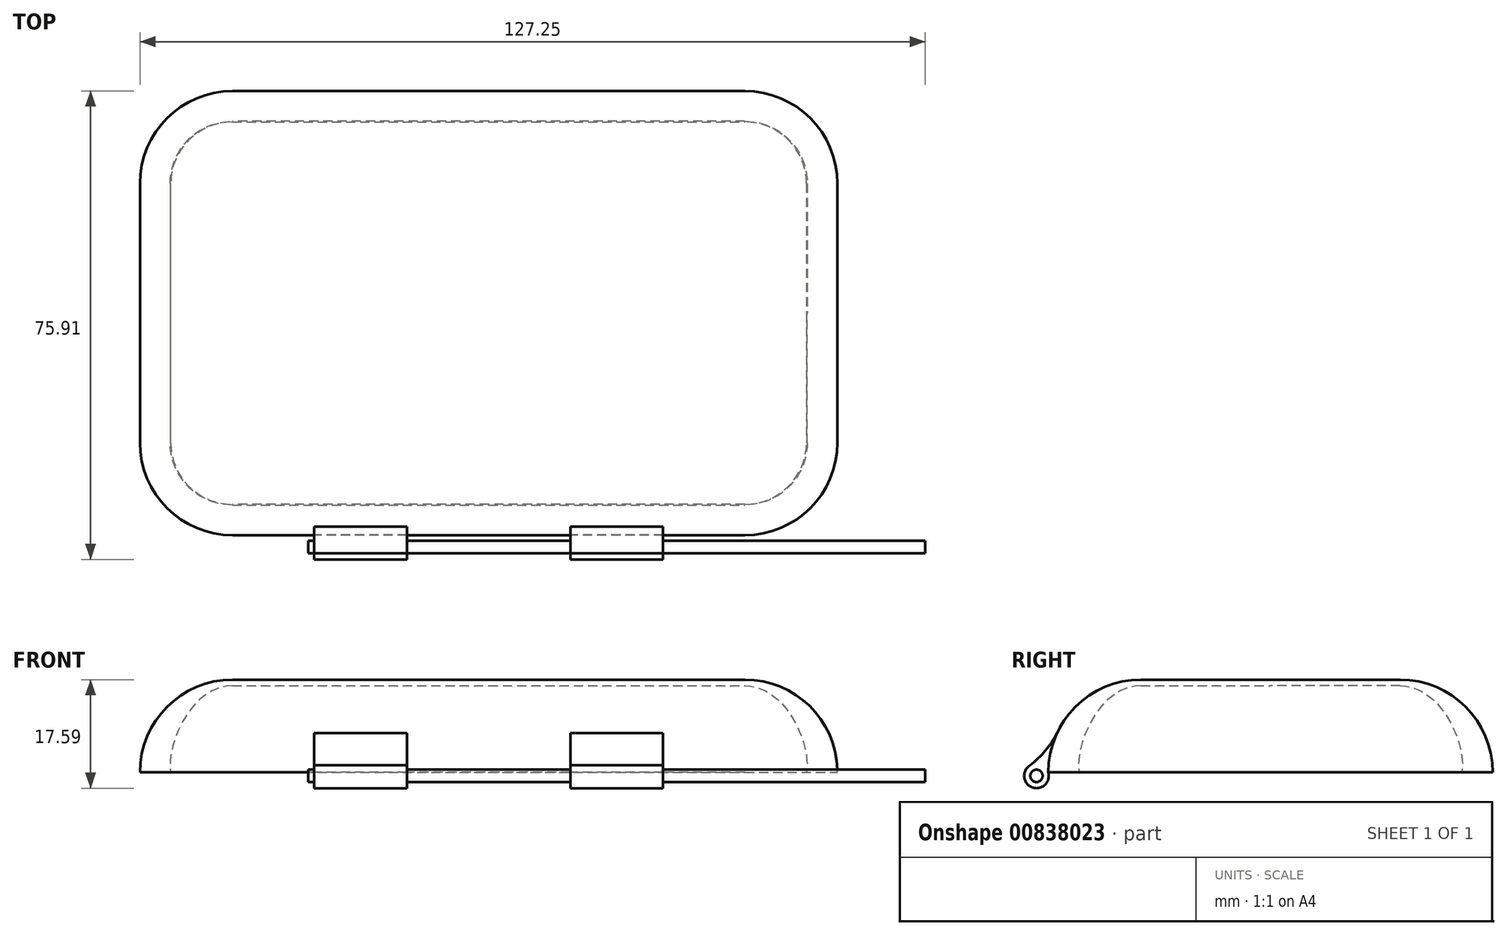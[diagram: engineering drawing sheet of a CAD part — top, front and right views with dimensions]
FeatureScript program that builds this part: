
annotation { "Feature Type Name" : "Feature", "Feature Type Description" : "" }
export const myFeature = defineFeature(function(context is Context, id is Id, definition is map)
    precondition{}
    {
        {
            var Q0;
            Q0=qCreatedBy(makeId("Top.planeOp"),FACE);
            var sketch = newSketch(context, id + "F0", { "sketchPlane" : qUnion([Q0])});
            skLineSegment(sketch, "E0", {"start": v(0, 0) * mm, "end": v(0, 27) * mm, "construction": true});
            skLineSegment(sketch, "E1", {"start": v(0, 27) * mm, "end": v(41.5, 27) * mm});
            skLineSegment(sketch, "E2", {"start": v(47.5, 21) * mm, "end": v(47.5, 0) * mm});
            skLineSegment(sketch, "E3", {"start": v(47.5, 0) * mm, "end": v(0, 0) * mm, "construction": true});
            skLineSegment(sketch, "E4.MirrorCS", {"start": v(0, 27) * mm, "end": v(-41.5, 27) * mm});
            skLineSegment(sketch, "E5.MirrorCS", {"start": v(-47.5, 21) * mm, "end": v(-47.5, 0) * mm});
            skLineSegment(sketch, "E6.MirrorCS", {"start": v(0, -27) * mm, "end": v(-41.5, -27) * mm});
            skLineSegment(sketch, "E7.MirrorCS", {"start": v(0, -27) * mm, "end": v(41.5, -27) * mm});
            skLineSegment(sketch, "E8.MirrorCS", {"start": v(47.5, -21) * mm, "end": v(47.5, 0) * mm});
            skLineSegment(sketch, "E9.MirrorCS", {"start": v(-47.5, -21) * mm, "end": v(-47.5, 0) * mm});
            skPoint(sketch, "E10.visualSharp", {"position": v(47.5, 27) * mm});
            skArc(sketch, "E10.filletArc", {"start": v(47.5, 21) * mm, "mid": v(45.74, 25.24) * mm, "end": v(41.5, 27) * mm});
            skPoint(sketch, "E11.visualSharp", {"position": v(-47.5, 27) * mm});
            skArc(sketch, "E11.filletArc", {"start": v(-41.5, 27) * mm, "mid": v(-45.74, 25.24) * mm, "end": v(-47.5, 21) * mm});
            skPoint(sketch, "E12.visualSharp", {"position": v(-47.5, -27) * mm});
            skArc(sketch, "E12.filletArc", {"start": v(-47.5, -21) * mm, "mid": v(-45.74, -25.24) * mm, "end": v(-41.5, -27) * mm});
            skPoint(sketch, "E13.visualSharp", {"position": v(47.5, -27) * mm});
            skArc(sketch, "E13.filletArc", {"start": v(41.5, -27) * mm, "mid": v(45.74, -25.24) * mm, "end": v(47.5, -21) * mm});
            skLineSegment(sketch, "E14.0", {"start": v(0, 31) * mm, "end": v(-41.5, 31) * mm});
            skArc(sketch, "E14.1", {"start": v(41.5, -31) * mm, "mid": v(48.57, -28.07) * mm, "end": v(51.5, -21) * mm});
            skLineSegment(sketch, "E14.2", {"start": v(51.5, -21) * mm, "end": v(51.5, 0) * mm});
            skLineSegment(sketch, "E14.3", {"start": v(51.5, 21) * mm, "end": v(51.5, 0) * mm});
            skArc(sketch, "E14.4", {"start": v(51.5, 21) * mm, "mid": v(48.57, 28.07) * mm, "end": v(41.5, 31) * mm});
            skLineSegment(sketch, "E14.5", {"start": v(0, -31) * mm, "end": v(41.5, -31) * mm});
            skLineSegment(sketch, "E14.6", {"start": v(0, 31) * mm, "end": v(41.5, 31) * mm});
            skLineSegment(sketch, "E14.7", {"start": v(0, -31) * mm, "end": v(-41.5, -31) * mm});
            skArc(sketch, "E14.8", {"start": v(-51.5, -21) * mm, "mid": v(-48.57, -28.07) * mm, "end": v(-41.5, -31) * mm});
            skLineSegment(sketch, "E14.9", {"start": v(-51.5, -21) * mm, "end": v(-51.5, 0) * mm});
            skLineSegment(sketch, "E14.10", {"start": v(-51.5, 21) * mm, "end": v(-51.5, 0) * mm});
            skArc(sketch, "E14.11", {"start": v(-41.5, 31) * mm, "mid": v(-48.57, 28.07) * mm, "end": v(-51.5, 21) * mm});
            skLineSegment(sketch, "E15", {"start": v(41.5, -21) * mm, "end": v(41.5, 21) * mm});
            skLineSegment(sketch, "E16", {"start": v(41.5, 21) * mm, "end": v(-41.5, 21) * mm});
            skLineSegment(sketch, "E17", {"start": v(-41.5, 21) * mm, "end": v(-41.5, -21) * mm});
            skLineSegment(sketch, "E18", {"start": v(-41.5, -21) * mm, "end": v(41.5, -21) * mm});
            skSolve(sketch);
        }
        {
            var Q0;
            Q0=qCreatedBy(makeId("Front.planeOp"),FACE);
            var sketch = newSketch(context, id + "F1", { "sketchPlane" : qUnion([Q0])});
            skArc(sketch, "E19", {"start": v(56.5, 0) * mm, "mid": v(52.1, 10.6) * mm, "end": v(41.5, 15) * mm});
            skFitSpline(sketch, "E20", {"points": [v(41.5, 14) * mm, v(51.5, 0) * mm, v(41.5, -12.07) * mm], "startDerivative": vector(40.14, 0) * mm, "endDerivative": vector(-25.73, -56.42) * mm});
            skLineSegment(sketch, "E21", {"start": v(41.5, 15) * mm, "end": v(41.5, 14) * mm});
            skLineSegment(sketch, "E22", {"start": v(41.5, 14) * mm, "end": v(41.5, 0) * mm, "construction": true});
            skLineSegment(sketch, "E23", {"start": v(56.5, 0) * mm, "end": v(51.5, 0) * mm});
            skSolve(sketch);
        }
        {
            var Q0;
            Q0=makeQuery(id+"F1.imprint","IMPRINT",FACE,{"disambiguationData":[TD([[makeQuery(id+"F1.imprint","IMPRINT",EDGE,{"derivedFrom":sQuery(id+"F1.wireOp",EDGE,"E19")}),1.0]])]});
            var Q1;
            Q1=sQuery(id+"F0.wireOp",EDGE,"E14.2");
            var Q2;
            Q2=sQuery(id+"F0.wireOp",EDGE,"E14.1");
            var Q3;
            Q3=sQuery(id+"F0.wireOp",EDGE,"E14.5");
            var Q4;
            Q4=sQuery(id+"F0.wireOp",EDGE,"E14.7");
            var Q5;
            Q5=sQuery(id+"F0.wireOp",EDGE,"E14.8");
            var Q6;
            Q6=sQuery(id+"F0.wireOp",EDGE,"E14.9");
            var Q7;
            Q7=sQuery(id+"F0.wireOp",EDGE,"E14.10");
            var Q8;
            Q8=sQuery(id+"F0.wireOp",EDGE,"E14.11");
            var Q9;
            Q9=sQuery(id+"F0.wireOp",EDGE,"E14.0");
            var Q10;
            Q10=sQuery(id+"F0.wireOp",EDGE,"E14.6");
            var Q11;
            Q11=sQuery(id+"F0.wireOp",EDGE,"E14.4");
            var Q12;
            Q12=sQuery(id+"F0.wireOp",EDGE,"E14.3");
            sweep(context, id + "F2", {"profiles" : qUnion([Q0]), "path" : qUnion([Q1, Q2, Q3, Q4, Q5, Q6, Q7, Q8, Q9, Q10, Q11, Q12])});
        }
        {
            var Q0;
            Q0=makeQuery(id+"F0.imprint","IMPRINT",FACE,{"disambiguationData":[TD([[makeQuery(id+"F0.imprint","IMPRINT",EDGE,{"derivedFrom":sQuery(id+"F0.wireOp",EDGE,"E15")}),1.0]])]});
            extrude(context, id + "F3", {"entities" : qUnion([Q0]), "operationType" : NewBodyOperationType.ADD, "depth" : 15 * mm, "offsetDistance" : 25 * mm, "hasSecondDirection" : true, "secondDirectionOppositeDirection" : false, "secondDirectionDepth" : 14 * mm});
        }
        {
            var Q0;
            Q0=makeQuery(id+"F3.opExtrude","CAP_FACE",FACE,{"disambiguationData":[OSD([sQuery(id+"F0.wireOp",EDGE,"E15"),sQuery(id+"F0.wireOp",EDGE,"E16"),sQuery(id+"F0.wireOp",EDGE,"E17"),sQuery(id+"F0.wireOp",EDGE,"E18")])],"isStart":false});
            var sketch = newSketch(context, id + "F4", { "sketchPlane" : qUnion([Q0])});
            skLineSegment(sketch, "E24", {"start": v(-41.5, -21) * mm, "end": v(0, -21) * mm, "construction": true});
            skPoint(sketch, "E25", {"position": v(0, -21) * mm});
            skPoint(sketch, "E26", {"position": v(-20.75, -21) * mm});
            skLineSegment(sketch, "E27", {"start": v(0, -21) * mm, "end": v(41.5, -21) * mm, "construction": true});
            skPoint(sketch, "E28", {"position": v(20.75, -21) * mm});
            skSolve(sketch);
        }
        {
            var Q0;
            Q0=sQuery(id+"F4.wireOp",VERTEX,"E28");
            var Q1;
            Q1=qCreatedBy(makeId("Right.planeOp"),FACE);
            cPlane(context, id + "F5", {"entities" : qUnion([Q0, Q1]), "cplaneType" : CPlaneType.PLANE_POINT, "offset" : 25 * mm, "width" : 150 * mm, "height" : 150 * mm});
        }
        {
            var Q0;
            Q0=sQuery(id+"F4.wireOp",EDGE,"E24");
            cPoint(context, id + "F6", {"entities" : qUnion([Q0]), "parameter" : 0.5});
        }
        {
            var Q0;
            Q0 = qCreatedBy(id + "F6" ,VERTEX);
            var Q1;
            Q1=qCreatedBy(makeId("Right.planeOp"),FACE);
            cPlane(context, id + "F7", {"entities" : qUnion([Q0, Q1]), "cplaneType" : CPlaneType.PLANE_POINT, "offset" : 25 * mm, "width" : 150 * mm, "height" : 150 * mm});
        }
        {
            var Q0;
            Q0=qCreatedBy(id+"F7.planeOp",FACE);
            var sketch = newSketch(context, id + "F8", { "sketchPlane" : qUnion([Q0])});
            skPoint(sketch, "E29", {"position": v(-21, 15) * mm});
            skPoint(sketch, "E30", {"position": v(-36, 0) * mm});
            skLineSegment(sketch, "E31", {"start": v(-21, 15) * mm, "end": v(-21, 0) * mm});
            skLineSegment(sketch, "E32", {"start": v(-36, 0) * mm, "end": v(-21, 0) * mm, "construction": true});
            skArc(sketch, "E33", {"start": v(-34.59, 6.35) * mm, "mid": v(-35.64, 3.25) * mm, "end": v(-36, 0) * mm});
            skLineSegment(sketch, "E34", {"start": v(-21, 0) * mm, "end": v(-40.9, -0.7) * mm, "construction": true});
            skCircle(sketch, "E35", {"center": v(-37.91, -0.6) * mm, "radius": 2 * mm});
            skArc(sketch, "E36", {"start": v(-38.95, 1.12) * mm, "mid": v(-36.48, 3.5) * mm, "end": v(-34.59, 6.35) * mm});
            skPoint(sketch, "E37", {"position": v(-34.59, 6.35) * mm});
            skLineSegment(sketch, "E38", {"start": v(-21, 0) * mm, "end": v(-36, 0) * mm});
            skCircle(sketch, "E39", {"center": v(-37.91, -0.6) * mm, "radius": 1 * mm});
            skSolve(sketch);
        }
        {
            var Q0;
            Q0 = qSketchRegion(id + "F8", true);
            extrude(context, id + "F9", {"entities" : qUnion([Q0]), "operationType" : NewBodyOperationType.ADD, "depth" : 15 * mm, "offsetDistance" : 25 * mm, "symmetric" : true});
        }
        {
            var Q0;
            Q0=qCreatedBy(id+"F5.planeOp",FACE);
            var sketch = newSketch(context, id + "F10", { "sketchPlane" : qUnion([Q0])});
            skPoint(sketch, "E40", {"position": v(-21, 15) * mm});
            skPoint(sketch, "E41", {"position": v(-36, 0) * mm});
            skLineSegment(sketch, "E42", {"start": v(-21, 15) * mm, "end": v(-21, 0) * mm, "construction": true});
            skLineSegment(sketch, "E43", {"start": v(-36, 0) * mm, "end": v(-21, 0) * mm, "construction": true});
            skArc(sketch, "E44", {"start": v(-21, 15) * mm, "mid": v(-31.6, 10.6) * mm, "end": v(-36, 0) * mm});
            skLineSegment(sketch, "E45", {"start": v(-21, 0) * mm, "end": v(-40.9, -0.7) * mm, "construction": true});
            skCircle(sketch, "E46", {"center": v(-37.91, -0.6) * mm, "radius": 2 * mm});
            skArc(sketch, "E47", {"start": v(-38.95, 1.12) * mm, "mid": v(-36.48, 3.5) * mm, "end": v(-34.59, 6.35) * mm});
            skPoint(sketch, "E48", {"position": v(-34.59, 6.35) * mm});
            skLineSegment(sketch, "E49", {"start": v(-21, 15) * mm, "end": v(-21, -9.72) * mm, "construction": true});
            skCircle(sketch, "E50", {"center": v(-37.91, -0.6) * mm, "radius": 1 * mm});
            skSolve(sketch);
        }
        {
            var Q0;
            {var subQ3=sQuery(id+"F10.wireOp",EDGE,"E47");Q0=makeQuery(id+"F10.imprint","IMPRINT",FACE,{"disambiguationData":[TD([[makeQuery(id+"F10.imprint","IMPRINT",EDGE,{"derivedFrom":subQ3}),-1.0]])]});}
            var Q1;
            {var subQ0=sQuery(id+"F10.wireOp",EDGE,"E46");var subQ1=makeQuery(id+"F10.imprint","INTERSECT",VERTEX,{"derivedFrom":[sQuery(id+"F10.wireOp",EDGE,"E44"),subQ0]});Q1=makeQuery(id+"F10.imprint","IMPRINT",FACE,{"disambiguationData":[TD([[makeQuery(id+"F10.imprint","IMPRINT",EDGE,{"disambiguationData":[TD([[subQ1,-1.0]])],"derivedFrom":subQ0}),1.0]])]});}
            extrude(context, id + "F11", {"entities" : qUnion([Q0, Q1]), "operationType" : NewBodyOperationType.ADD, "depth" : 15 * mm, "offsetDistance" : 25 * mm, "symmetric" : true});
        }
        {
            var Q0;
            Q0=makeQuery(id+"F10.imprint","IMPRINT",FACE,{"disambiguationData":[TD([[makeQuery(id+"F10.imprint","IMPRINT",EDGE,{"derivedFrom":sQuery(id+"F10.wireOp",EDGE,"E50")}),1.0]])]});
            extrude(context, id + "F12", {"entities" : qUnion([Q0]), "operationType" : NewBodyOperationType.ADD, "oppositeDirection" : true, "depth" : 100 * mm, "offsetDistance" : 25 * mm, "symmetric" : true});
        }
    });
